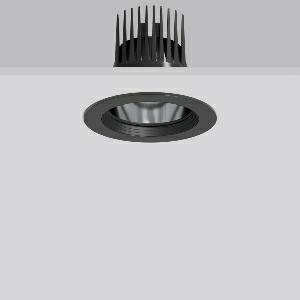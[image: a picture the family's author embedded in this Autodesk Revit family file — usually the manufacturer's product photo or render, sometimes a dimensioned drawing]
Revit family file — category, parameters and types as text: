
# Revit family: heledon_maxi_e_901765_003_2_76_7819
name_source: partatom
category: Lighting Fixtures
units: mm (PartAtom-declared; Revit-internal decimal feet)

## family parameters
Cut with Voids When Loaded = No
Host = Face
Light Source = No
Part Type = Normal
Room Calculation Point = No
Round Connector Dimension = Use Diameter
Shared = No

## types (1)
- HELEDON maxi E (1 x LED Modul 927, 4100 lm, 2700)
    Apparent Load = 35 VA
    Approval mark = CE
    CIE Flux Codes = 100 100 100 100 100
    Color Rendering = 92
    Color Temperature = 2700
    Default Elevation = 1800 mm
    Description = Series: HELEDON maxi
Round recessed downlight. Housing: die-cast aluminium, powder-coated. Black plastic ring and recessed LED to prevent glare from the side. Optical assembly with reflector made of MIRO-Silver with 98% total light reflection for outstanding efficiency - can be changed without tools. Best colour rendering index Ra>90. Suitable for Recessed ceiling mounting. Installation without tools thanks to spring fastening system. Including separate LED converter with connecting cable 600 mm.High quality converter without flickering and stroboscopic effect. Through-wiring box (5 pole) available as accessory. The following accessories can be mounted without use of tools: interchangeable lenses, decorative glasses, honeycomb louvre, clear and frosted diffusers, white interchangeable plastic ring. 
Colour: deep black, matt (RAL 9005)
Diameter: 162 mm
Height: 3 mm
Cut-out diameter: 152 mm
Recess height: 200 mm
Luminaire: recess height: 135 mm
Lamp: LED
Socket: without socket
Colour temperature: 2700K
Colour rendering index (CRI): 92
System power: 35 W
Rated luminous flux: 4100 lm
Luminous efficiency: 117 lm/W
Control gear: Converter, dimmable, DALI
Protection class: II
Type of protection: IP 20
    Height = 0 mm  [stored 0 ft]
    Lamp = 1 x LED Modul 927
    Lamp Light Flux = 4100 lm
    Lamp count = 1
    Length = 162 mm
    Lifetime = 50000 h
    Luminous efficacy = 117 lm/W
    Manufacturer = RZB
    ModVariant = No
    Model = 901765.003.2.76
    Mounting Place = Ceiling
    Mounting Type = Recessed
    Number of Poles = 1
    OnlyDefault = Yes
    Power Factor = 1
    Product Name = HELEDON maxi E
    Product group = Recessed downlights
    ProductGroupID = 402
    Protection Class = Protection class II
    Protection Degree = IP 20
    RLX_Detail_Level = 1
    RLX_Emergency_Light_Flux = 0 lm
    RLX_Emergency_Type = 0
    RLX_Emergency_Type_DB = No
    RlxData = <blob elided: 119605 chars, md5=42bbecfc>
    Socket = socket
    Standby Power = 0 W
    System Light Flux = 4100 lm
    System Power = 35 W
    Type Comments = Product without accessories
    Type Image = 901662.003.jpg
    URL = http://relux.com
    VarID = ---
    Voltage = 230 V
    Voltage Range = 220-240 V
    Weight = 0.00 kg
    Width = 0 mm  [stored 0 ft]

note: [stored X ft] marks values corroborated as IEEE doubles in the binary element streams (Revit-internal decimal feet)

## geometry (parser evidence)
native form markers: Blend x4, Sweep x13
no freeform markers — native parametric forms only
